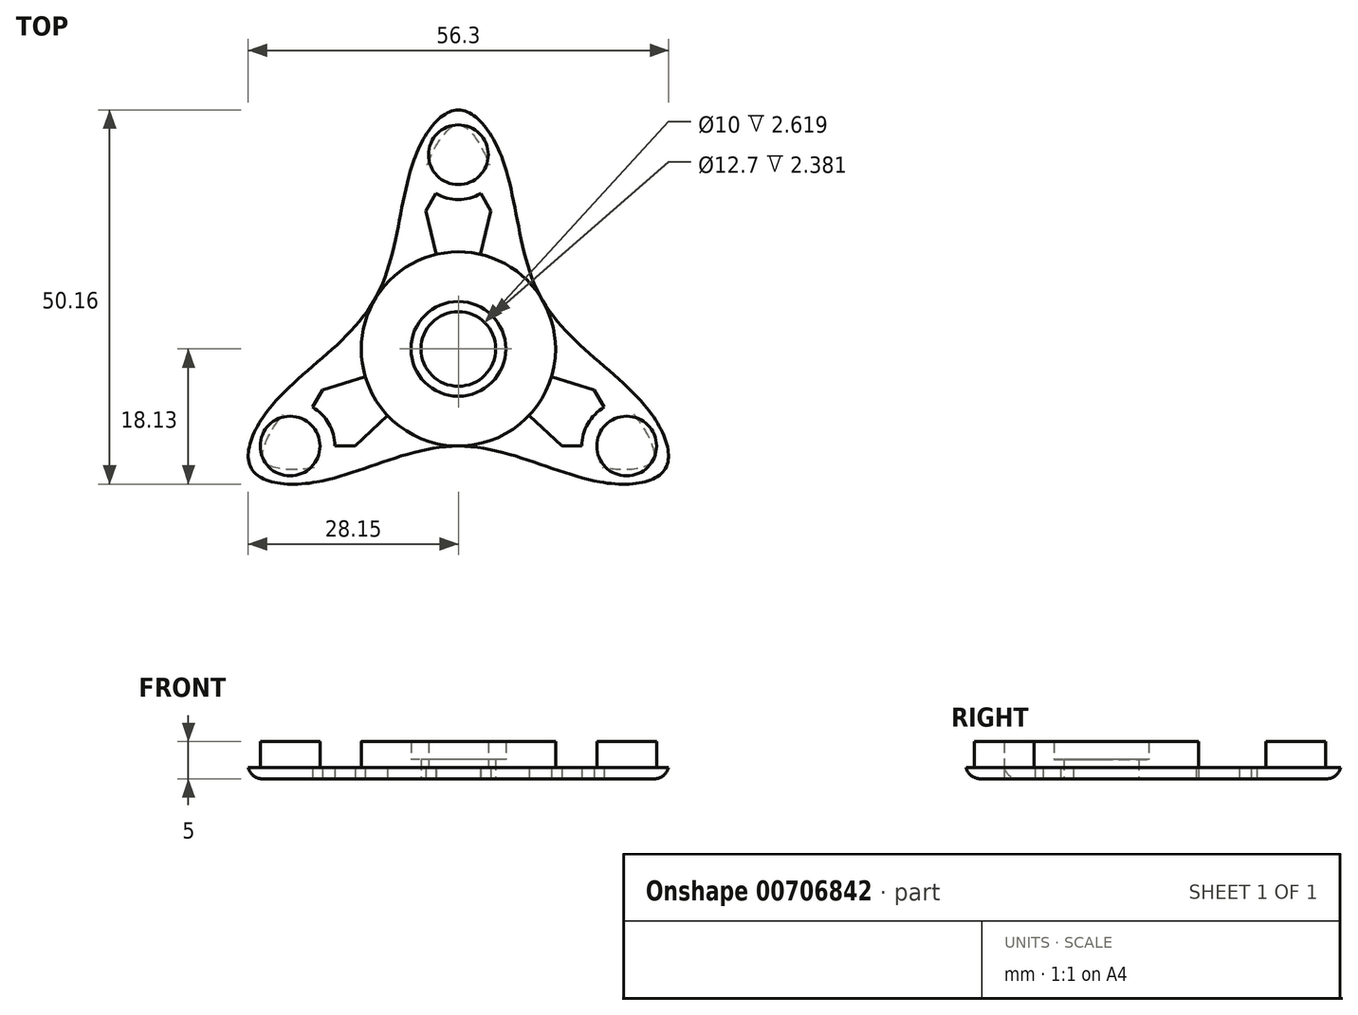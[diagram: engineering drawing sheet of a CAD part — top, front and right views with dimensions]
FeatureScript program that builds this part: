
annotation { "Feature Type Name" : "Feature", "Feature Type Description" : "" }
export const myFeature = defineFeature(function(context is Context, id is Id, definition is map)
    precondition{}
    {
        {
            var Q0;
            Q0=qCreatedBy(makeId("Top.planeOp"),FACE);
            var sketch = newSketch(context, id + "F0", { "sketchPlane" : qUnion([Q0])});
            skCircle(sketch, "E0", {"center": v(0, 0) * mm, "radius": 6.35 * mm});
            skCircle(sketch, "E1", {"center": v(0, 0) * mm, "radius": 26.03 * mm});
            skLineSegment(sketch, "E2", {"start": v(0, 0) * mm, "end": v(22.54, -13.01) * mm});
            skLineSegment(sketch, "E3", {"start": v(0, 0) * mm, "end": v(0, 26.03) * mm});
            skLineSegment(sketch, "E4", {"start": v(0, 26.03) * mm, "end": v(-22.54, -13.01) * mm});
            skLineSegment(sketch, "E5", {"start": v(0, 26.03) * mm, "end": v(22.54, -13.01) * mm});
            skLineSegment(sketch, "E6", {"start": v(22.54, -13.01) * mm, "end": v(-22.54, -13.01) * mm});
            skLineSegment(sketch, "E7", {"start": v(0, 0) * mm, "end": v(-22.54, -13.01) * mm});
            skCircle(sketch, "E8", {"center": v(0, 26.03) * mm, "radius": 4 * mm});
            skCircle(sketch, "E9", {"center": v(22.54, -13.01) * mm, "radius": 4 * mm});
            skCircle(sketch, "E10", {"center": v(-22.54, -13.01) * mm, "radius": 4 * mm});
            skLineSegment(sketch, "E11", {"start": v(0, 0) * mm, "end": v(-11.27, 6.5) * mm});
            skLineSegment(sketch, "E12", {"start": v(0, 0) * mm, "end": v(0, -13.01) * mm});
            skLineSegment(sketch, "E13", {"start": v(0, 0) * mm, "end": v(11.27, 6.5) * mm});
            skCircle(sketch, "E14", {"center": v(-22.54, -13.01) * mm, "radius": 6 * mm});
            skCircle(sketch, "E15", {"center": v(22.54, -13.01) * mm, "radius": 6 * mm});
            skCircle(sketch, "E16", {"center": v(0, 26.03) * mm, "radius": 6 * mm});
            skLineSegment(sketch, "E17", {"start": v(-24.92, -7.5) * mm, "end": v(0, 0) * mm});
            skLineSegment(sketch, "E18", {"start": v(-18.96, -17.83) * mm, "end": v(0, 0) * mm});
            skLineSegment(sketch, "E19", {"start": v(24.92, -7.5) * mm, "end": v(0, 0) * mm});
            skLineSegment(sketch, "E20", {"start": v(18.96, -17.83) * mm, "end": v(0, 0) * mm});
            skLineSegment(sketch, "E21", {"start": v(-5.96, 25.34) * mm, "end": v(0, 0) * mm});
            skLineSegment(sketch, "E22", {"start": v(5.96, 25.34) * mm, "end": v(0, 0) * mm});
            skLineSegment(sketch, "E23", {"start": v(0, 32.03) * mm, "end": v(0, 0) * mm});
            skLineSegment(sketch, "E24", {"start": v(0, 0) * mm, "end": v(-27.74, -16.01) * mm});
            skLineSegment(sketch, "E25", {"start": v(0, 0) * mm, "end": v(27.74, -16.01) * mm});
            skFitSpline(sketch, "E26", {"points": [v(-11.27, 6.5) * mm, v(-5.96, 25.34) * mm, v(0, 32.03) * mm, v(5.96, 25.34) * mm, v(11.27, 6.5) * mm, v(24.92, -7.5) * mm, v(27.74, -16.01) * mm, v(18.96, -17.83) * mm, v(0, -13.01) * mm, v(-18.96, -17.83) * mm, v(-27.74, -16.01) * mm, v(-24.92, -7.5) * mm, v(-11.27, 6.5) * mm]});
            skCircle(sketch, "E27", {"center": v(0, 0) * mm, "radius": 13.01 * mm});
            skCircle(sketch, "E28", {"center": v(0, 0) * mm, "radius": 5 * mm});
            skSolve(sketch);
        }
        {
            var Q0;
            {var subQ2=sQuery(id+"F0.wireOp",EDGE,"E1");var subQ4=sQuery(id+"F0.wireOp",EDGE,"E10");var subQ5=makeQuery(id+"F0.imprint","INTERSECT",VERTEX,{"disambiguationData":[OD(0.0)],"derivedFrom":[subQ2,subQ4]});Q0=makeQuery(id+"F0.imprint","IMPRINT",FACE,{"disambiguationData":[TD([[makeQuery(id+"F0.imprint","IMPRINT",EDGE,{"disambiguationData":[TD([[subQ5,-1.0]])],"derivedFrom":subQ4}),-1.0]])]});}
            var Q1;
            {var subQ2=sQuery(id+"F0.wireOp",EDGE,"E1");var subQ4=sQuery(id+"F0.wireOp",EDGE,"E10");var subQ5=makeQuery(id+"F0.imprint","INTERSECT",VERTEX,{"disambiguationData":[OD(1.0)],"derivedFrom":[subQ2,subQ4]});Q1=makeQuery(id+"F0.imprint","IMPRINT",FACE,{"disambiguationData":[TD([[makeQuery(id+"F0.imprint","IMPRINT",EDGE,{"disambiguationData":[TD([[subQ5,1.0]])],"derivedFrom":subQ4}),-1.0]])]});}
            var Q2;
            {var subQ0=sQuery(id+"F0.wireOp",EDGE,"E14");var subQ1=sQuery(id+"F0.wireOp",EDGE,"E6");var subQ2=makeQuery(id+"F0.imprint","INTERSECT",VERTEX,{"derivedFrom":[subQ1,subQ0]});Q2=makeQuery(id+"F0.imprint","IMPRINT",FACE,{"disambiguationData":[TD([[makeQuery(id+"F0.imprint","IMPRINT",EDGE,{"disambiguationData":[TD([[subQ2,-1.0]])],"derivedFrom":subQ1}),1.0]])]});}
            var Q3;
            {var subQ0=sQuery(id+"F0.wireOp",EDGE,"E14");var subQ1=sQuery(id+"F0.wireOp",EDGE,"E6");var subQ2=makeQuery(id+"F0.imprint","INTERSECT",VERTEX,{"derivedFrom":[subQ1,subQ0]});Q3=makeQuery(id+"F0.imprint","IMPRINT",FACE,{"disambiguationData":[TD([[makeQuery(id+"F0.imprint","IMPRINT",EDGE,{"disambiguationData":[TD([[subQ2,-1.0]])],"derivedFrom":subQ1}),-1.0]])]});}
            var Q4;
            {var subQ0=sQuery(id+"F0.wireOp",EDGE,"E14");var subQ1=sQuery(id+"F0.wireOp",EDGE,"E4");var subQ2=makeQuery(id+"F0.imprint","INTERSECT",VERTEX,{"derivedFrom":[subQ1,subQ0]});Q4=makeQuery(id+"F0.imprint","IMPRINT",FACE,{"disambiguationData":[TD([[makeQuery(id+"F0.imprint","IMPRINT",EDGE,{"disambiguationData":[TD([[subQ2,-1.0]])],"derivedFrom":subQ1}),1.0]])]});}
            var Q5;
            {var subQ3=sQuery(id+"F0.wireOp",EDGE,"E4");var subQ5=sQuery(id+"F0.wireOp",EDGE,"E14");var subQ6=makeQuery(id+"F0.imprint","INTERSECT",VERTEX,{"derivedFrom":[subQ3,subQ5]});Q5=makeQuery(id+"F0.imprint","IMPRINT",FACE,{"disambiguationData":[TD([[makeQuery(id+"F0.imprint","IMPRINT",EDGE,{"disambiguationData":[TD([[subQ6,-1.0]])],"derivedFrom":subQ3}),-1.0]])]});}
            var Q6;
            {var subQ0=sQuery(id+"F0.wireOp",EDGE,"E17");var subQ1=sQuery(id+"F0.wireOp",EDGE,"E4");var subQ2=makeQuery(id+"F0.imprint","INTERSECT",VERTEX,{"derivedFrom":[subQ1,subQ0]});Q6=makeQuery(id+"F0.imprint","IMPRINT",FACE,{"disambiguationData":[TD([[makeQuery(id+"F0.imprint","IMPRINT",EDGE,{"disambiguationData":[TD([[subQ2,-1.0]])],"derivedFrom":subQ1}),-1.0]])]});}
            var Q7;
            {var subQ0=sQuery(id+"F0.wireOp",EDGE,"E18");var subQ1=sQuery(id+"F0.wireOp",EDGE,"E6");var subQ2=makeQuery(id+"F0.imprint","INTERSECT",VERTEX,{"derivedFrom":[subQ1,subQ0]});Q7=makeQuery(id+"F0.imprint","IMPRINT",FACE,{"disambiguationData":[TD([[makeQuery(id+"F0.imprint","IMPRINT",EDGE,{"disambiguationData":[TD([[subQ2,-1.0]])],"derivedFrom":subQ1}),1.0]])]});}
            var Q8;
            {var subQ0=sQuery(id+"F0.wireOp",EDGE,"E17");var subQ1=sQuery(id+"F0.wireOp",EDGE,"E0");var subQ2=makeQuery(id+"F0.imprint","INTERSECT",VERTEX,{"derivedFrom":[subQ1,subQ0]});Q8=makeQuery(id+"F0.imprint","IMPRINT",FACE,{"disambiguationData":[TD([[makeQuery(id+"F0.imprint","IMPRINT",EDGE,{"disambiguationData":[TD([[subQ2,-1.0]])],"derivedFrom":subQ1}),-1.0]])]});}
            var Q9;
            {var subQ0=sQuery(id+"F0.wireOp",EDGE,"E24");var subQ1=sQuery(id+"F0.wireOp",EDGE,"E0");var subQ2=makeQuery(id+"F0.imprint","INTERSECT",VERTEX,{"derivedFrom":[subQ1,subQ0]});Q9=makeQuery(id+"F0.imprint","IMPRINT",FACE,{"disambiguationData":[TD([[makeQuery(id+"F0.imprint","IMPRINT",EDGE,{"disambiguationData":[TD([[subQ2,-1.0]])],"derivedFrom":subQ1}),-1.0]])]});}
            var Q10;
            {var subQ0=sQuery(id+"F0.wireOp",EDGE,"E11");var subQ1=sQuery(id+"F0.wireOp",EDGE,"E0");var subQ2=makeQuery(id+"F0.imprint","INTERSECT",VERTEX,{"derivedFrom":[subQ1,subQ0]});Q10=makeQuery(id+"F0.imprint","IMPRINT",FACE,{"disambiguationData":[TD([[makeQuery(id+"F0.imprint","IMPRINT",EDGE,{"disambiguationData":[TD([[subQ2,-1.0]])],"derivedFrom":subQ1}),-1.0]])]});}
            var Q11;
            {var subQ0=sQuery(id+"F0.wireOp",EDGE,"E18");var subQ1=sQuery(id+"F0.wireOp",EDGE,"E0");var subQ2=makeQuery(id+"F0.imprint","INTERSECT",VERTEX,{"derivedFrom":[subQ1,subQ0]});Q11=makeQuery(id+"F0.imprint","IMPRINT",FACE,{"disambiguationData":[TD([[makeQuery(id+"F0.imprint","IMPRINT",EDGE,{"disambiguationData":[TD([[subQ2,-1.0]])],"derivedFrom":subQ1}),-1.0]])]});}
            var Q12;
            {var subQ0=sQuery(id+"F0.wireOp",EDGE,"E12");var subQ1=sQuery(id+"F0.wireOp",EDGE,"E0");var subQ2=makeQuery(id+"F0.imprint","INTERSECT",VERTEX,{"derivedFrom":[subQ1,subQ0]});Q12=makeQuery(id+"F0.imprint","IMPRINT",FACE,{"disambiguationData":[TD([[makeQuery(id+"F0.imprint","IMPRINT",EDGE,{"disambiguationData":[TD([[subQ2,-1.0]])],"derivedFrom":subQ1}),-1.0]])]});}
            var Q13;
            {var subQ0=sQuery(id+"F0.wireOp",EDGE,"E20");var subQ1=sQuery(id+"F0.wireOp",EDGE,"E0");var subQ2=makeQuery(id+"F0.imprint","INTERSECT",VERTEX,{"derivedFrom":[subQ1,subQ0]});Q13=makeQuery(id+"F0.imprint","IMPRINT",FACE,{"disambiguationData":[TD([[makeQuery(id+"F0.imprint","IMPRINT",EDGE,{"disambiguationData":[TD([[subQ2,-1.0]])],"derivedFrom":subQ1}),-1.0]])]});}
            var Q14;
            {var subQ0=sQuery(id+"F0.wireOp",EDGE,"E25");var subQ1=sQuery(id+"F0.wireOp",EDGE,"E0");var subQ2=makeQuery(id+"F0.imprint","INTERSECT",VERTEX,{"derivedFrom":[subQ1,subQ0]});Q14=makeQuery(id+"F0.imprint","IMPRINT",FACE,{"disambiguationData":[TD([[makeQuery(id+"F0.imprint","IMPRINT",EDGE,{"disambiguationData":[TD([[subQ2,-1.0]])],"derivedFrom":subQ1}),-1.0]])]});}
            var Q15;
            {var subQ0=sQuery(id+"F0.wireOp",EDGE,"E13");var subQ1=sQuery(id+"F0.wireOp",EDGE,"E0");var subQ2=makeQuery(id+"F0.imprint","INTERSECT",VERTEX,{"derivedFrom":[subQ1,subQ0]});Q15=makeQuery(id+"F0.imprint","IMPRINT",FACE,{"disambiguationData":[TD([[makeQuery(id+"F0.imprint","IMPRINT",EDGE,{"disambiguationData":[TD([[subQ2,1.0]])],"derivedFrom":subQ1}),-1.0]])]});}
            var Q16;
            {var subQ0=sQuery(id+"F0.wireOp",EDGE,"E22");var subQ1=sQuery(id+"F0.wireOp",EDGE,"E0");var subQ2=makeQuery(id+"F0.imprint","INTERSECT",VERTEX,{"derivedFrom":[subQ1,subQ0]});Q16=makeQuery(id+"F0.imprint","IMPRINT",FACE,{"disambiguationData":[TD([[makeQuery(id+"F0.imprint","IMPRINT",EDGE,{"disambiguationData":[TD([[subQ2,1.0]])],"derivedFrom":subQ1}),-1.0]])]});}
            var Q17;
            {var subQ0=sQuery(id+"F0.wireOp",EDGE,"E21");var subQ1=sQuery(id+"F0.wireOp",EDGE,"E0");var subQ2=makeQuery(id+"F0.imprint","INTERSECT",VERTEX,{"derivedFrom":[subQ1,subQ0]});Q17=makeQuery(id+"F0.imprint","IMPRINT",FACE,{"disambiguationData":[TD([[makeQuery(id+"F0.imprint","IMPRINT",EDGE,{"disambiguationData":[TD([[subQ2,-1.0]])],"derivedFrom":subQ1}),-1.0]])]});}
            var Q18;
            {var subQ0=sQuery(id+"F0.wireOp",EDGE,"E23");var subQ1=sQuery(id+"F0.wireOp",EDGE,"E0");var subQ2=makeQuery(id+"F0.imprint","INTERSECT",VERTEX,{"derivedFrom":[subQ1,subQ0]});Q18=makeQuery(id+"F0.imprint","IMPRINT",FACE,{"disambiguationData":[TD([[makeQuery(id+"F0.imprint","IMPRINT",EDGE,{"disambiguationData":[TD([[subQ2,-1.0]])],"derivedFrom":subQ1}),-1.0]])]});}
            var Q19;
            {var subQ0=sQuery(id+"F0.wireOp",EDGE,"E22");var subQ1=sQuery(id+"F0.wireOp",EDGE,"E0");var subQ2=makeQuery(id+"F0.imprint","INTERSECT",VERTEX,{"derivedFrom":[subQ1,subQ0]});Q19=makeQuery(id+"F0.imprint","IMPRINT",FACE,{"disambiguationData":[TD([[makeQuery(id+"F0.imprint","IMPRINT",EDGE,{"disambiguationData":[TD([[subQ2,-1.0]])],"derivedFrom":subQ1}),-1.0]])]});}
            var Q20;
            {var subQ1=sQuery(id+"F0.wireOp",EDGE,"E4");var subQ3=sQuery(id+"F0.wireOp",EDGE,"E17");var subQ4=makeQuery(id+"F0.imprint","INTERSECT",VERTEX,{"derivedFrom":[subQ1,subQ3]});Q20=makeQuery(id+"F0.imprint","IMPRINT",FACE,{"disambiguationData":[TD([[makeQuery(id+"F0.imprint","IMPRINT",EDGE,{"disambiguationData":[TD([[subQ4,-1.0]])],"derivedFrom":subQ3}),1.0]])]});}
            var Q21;
            {var subQ1=sQuery(id+"F0.wireOp",EDGE,"E6");var subQ3=sQuery(id+"F0.wireOp",EDGE,"E18");var subQ4=makeQuery(id+"F0.imprint","INTERSECT",VERTEX,{"derivedFrom":[subQ1,subQ3]});Q21=makeQuery(id+"F0.imprint","IMPRINT",FACE,{"disambiguationData":[TD([[makeQuery(id+"F0.imprint","IMPRINT",EDGE,{"disambiguationData":[TD([[subQ4,-1.0]])],"derivedFrom":subQ3}),-1.0]])]});}
            var Q22;
            {var subQ1=sQuery(id+"F0.wireOp",EDGE,"E6");var subQ3=sQuery(id+"F0.wireOp",EDGE,"E20");var subQ4=makeQuery(id+"F0.imprint","INTERSECT",VERTEX,{"derivedFrom":[subQ1,subQ3]});Q22=makeQuery(id+"F0.imprint","IMPRINT",FACE,{"disambiguationData":[TD([[makeQuery(id+"F0.imprint","IMPRINT",EDGE,{"disambiguationData":[TD([[subQ4,-1.0]])],"derivedFrom":subQ3}),1.0]])]});}
            var Q23;
            {var subQ0=sQuery(id+"F0.wireOp",EDGE,"E15");var subQ1=sQuery(id+"F0.wireOp",EDGE,"E5");var subQ2=makeQuery(id+"F0.imprint","INTERSECT",VERTEX,{"derivedFrom":[subQ1,subQ0]});Q23=makeQuery(id+"F0.imprint","IMPRINT",FACE,{"disambiguationData":[TD([[makeQuery(id+"F0.imprint","IMPRINT",EDGE,{"disambiguationData":[TD([[subQ2,-1.0]])],"derivedFrom":subQ1}),-1.0]])]});}
            var Q24;
            {var subQ0=sQuery(id+"F0.wireOp",EDGE,"E9");var subQ1=sQuery(id+"F0.wireOp",EDGE,"E6");var subQ2=makeQuery(id+"F0.imprint","INTERSECT",VERTEX,{"derivedFrom":[subQ1,subQ0]});Q24=makeQuery(id+"F0.imprint","IMPRINT",FACE,{"disambiguationData":[TD([[makeQuery(id+"F0.imprint","IMPRINT",EDGE,{"disambiguationData":[TD([[subQ2,-1.0]])],"derivedFrom":subQ1}),-1.0]])]});}
            var Q25;
            {var subQ0=sQuery(id+"F0.wireOp",EDGE,"E9");var subQ3=sQuery(id+"F0.wireOp",EDGE,"E6");var subQ4=makeQuery(id+"F0.imprint","INTERSECT",VERTEX,{"derivedFrom":[subQ3,subQ0]});Q25=makeQuery(id+"F0.imprint","IMPRINT",FACE,{"disambiguationData":[TD([[makeQuery(id+"F0.imprint","IMPRINT",EDGE,{"disambiguationData":[TD([[subQ4,-1.0]])],"derivedFrom":subQ3}),1.0]])]});}
            var Q26;
            {var subQ2=sQuery(id+"F0.wireOp",EDGE,"E1");var subQ4=sQuery(id+"F0.wireOp",EDGE,"E9");var subQ5=makeQuery(id+"F0.imprint","INTERSECT",VERTEX,{"disambiguationData":[OD(0.0)],"derivedFrom":[subQ2,subQ4]});Q26=makeQuery(id+"F0.imprint","IMPRINT",FACE,{"disambiguationData":[TD([[makeQuery(id+"F0.imprint","IMPRINT",EDGE,{"disambiguationData":[TD([[subQ5,-1.0]])],"derivedFrom":subQ4}),-1.0]])]});}
            var Q27;
            {var subQ2=sQuery(id+"F0.wireOp",EDGE,"E1");var subQ4=sQuery(id+"F0.wireOp",EDGE,"E9");var subQ5=makeQuery(id+"F0.imprint","INTERSECT",VERTEX,{"disambiguationData":[OD(1.0)],"derivedFrom":[subQ2,subQ4]});Q27=makeQuery(id+"F0.imprint","IMPRINT",FACE,{"disambiguationData":[TD([[makeQuery(id+"F0.imprint","IMPRINT",EDGE,{"disambiguationData":[TD([[subQ5,1.0]])],"derivedFrom":subQ4}),-1.0]])]});}
            var Q28;
            {var subQ0=sQuery(id+"F0.wireOp",EDGE,"E15");var subQ1=sQuery(id+"F0.wireOp",EDGE,"E5");var subQ2=makeQuery(id+"F0.imprint","INTERSECT",VERTEX,{"derivedFrom":[subQ1,subQ0]});Q28=makeQuery(id+"F0.imprint","IMPRINT",FACE,{"disambiguationData":[TD([[makeQuery(id+"F0.imprint","IMPRINT",EDGE,{"disambiguationData":[TD([[subQ2,-1.0]])],"derivedFrom":subQ1}),1.0]])]});}
            var Q29;
            {var subQ0=sQuery(id+"F0.wireOp",EDGE,"E19");var subQ1=sQuery(id+"F0.wireOp",EDGE,"E5");var subQ2=makeQuery(id+"F0.imprint","INTERSECT",VERTEX,{"derivedFrom":[subQ1,subQ0]});Q29=makeQuery(id+"F0.imprint","IMPRINT",FACE,{"disambiguationData":[TD([[makeQuery(id+"F0.imprint","IMPRINT",EDGE,{"disambiguationData":[TD([[subQ2,-1.0]])],"derivedFrom":subQ1}),1.0]])]});}
            var Q30;
            {var subQ1=sQuery(id+"F0.wireOp",EDGE,"E5");var subQ3=sQuery(id+"F0.wireOp",EDGE,"E19");var subQ4=makeQuery(id+"F0.imprint","INTERSECT",VERTEX,{"derivedFrom":[subQ1,subQ3]});Q30=makeQuery(id+"F0.imprint","IMPRINT",FACE,{"disambiguationData":[TD([[makeQuery(id+"F0.imprint","IMPRINT",EDGE,{"disambiguationData":[TD([[subQ4,-1.0]])],"derivedFrom":subQ3}),-1.0]])]});}
            var Q31;
            {var subQ1=sQuery(id+"F0.wireOp",EDGE,"E4");var subQ3=sQuery(id+"F0.wireOp",EDGE,"E21");var subQ4=makeQuery(id+"F0.imprint","INTERSECT",VERTEX,{"derivedFrom":[subQ1,subQ3]});Q31=makeQuery(id+"F0.imprint","IMPRINT",FACE,{"disambiguationData":[TD([[makeQuery(id+"F0.imprint","IMPRINT",EDGE,{"disambiguationData":[TD([[subQ4,-1.0]])],"derivedFrom":subQ3}),-1.0]])]});}
            var Q32;
            {var subQ0=sQuery(id+"F0.wireOp",EDGE,"E8");var subQ3=sQuery(id+"F0.wireOp",EDGE,"E5");var subQ4=makeQuery(id+"F0.imprint","INTERSECT",VERTEX,{"derivedFrom":[subQ3,subQ0]});Q32=makeQuery(id+"F0.imprint","IMPRINT",FACE,{"disambiguationData":[TD([[makeQuery(id+"F0.imprint","IMPRINT",EDGE,{"disambiguationData":[TD([[subQ4,-1.0]])],"derivedFrom":subQ3}),1.0]])]});}
            var Q33;
            {var subQ0=sQuery(id+"F0.wireOp",EDGE,"E8");var subQ1=sQuery(id+"F0.wireOp",EDGE,"E5");var subQ2=makeQuery(id+"F0.imprint","INTERSECT",VERTEX,{"derivedFrom":[subQ1,subQ0]});Q33=makeQuery(id+"F0.imprint","IMPRINT",FACE,{"disambiguationData":[TD([[makeQuery(id+"F0.imprint","IMPRINT",EDGE,{"disambiguationData":[TD([[subQ2,-1.0]])],"derivedFrom":subQ1}),-1.0]])]});}
            var Q34;
            {var subQ0=sQuery(id+"F0.wireOp",EDGE,"E16");var subQ1=sQuery(id+"F0.wireOp",EDGE,"E4");var subQ2=makeQuery(id+"F0.imprint","INTERSECT",VERTEX,{"derivedFrom":[subQ1,subQ0]});Q34=makeQuery(id+"F0.imprint","IMPRINT",FACE,{"disambiguationData":[TD([[makeQuery(id+"F0.imprint","IMPRINT",EDGE,{"disambiguationData":[TD([[subQ2,-1.0]])],"derivedFrom":subQ1}),-1.0]])]});}
            var Q35;
            {var subQ2=sQuery(id+"F0.wireOp",EDGE,"E1");var subQ4=sQuery(id+"F0.wireOp",EDGE,"E8");var subQ5=makeQuery(id+"F0.imprint","INTERSECT",VERTEX,{"disambiguationData":[OD(1.0)],"derivedFrom":[subQ2,subQ4]});Q35=makeQuery(id+"F0.imprint","IMPRINT",FACE,{"disambiguationData":[TD([[makeQuery(id+"F0.imprint","IMPRINT",EDGE,{"disambiguationData":[TD([[subQ5,1.0]])],"derivedFrom":subQ4}),-1.0]])]});}
            var Q36;
            {var subQ2=sQuery(id+"F0.wireOp",EDGE,"E1");var subQ4=sQuery(id+"F0.wireOp",EDGE,"E8");var subQ5=makeQuery(id+"F0.imprint","INTERSECT",VERTEX,{"disambiguationData":[OD(0.0)],"derivedFrom":[subQ2,subQ4]});Q36=makeQuery(id+"F0.imprint","IMPRINT",FACE,{"disambiguationData":[TD([[makeQuery(id+"F0.imprint","IMPRINT",EDGE,{"disambiguationData":[TD([[subQ5,-1.0]])],"derivedFrom":subQ4}),-1.0]])]});}
            var Q37;
            {var subQ0=sQuery(id+"F0.wireOp",EDGE,"E15");var subQ1=sQuery(id+"F0.wireOp",EDGE,"E6");var subQ2=makeQuery(id+"F0.imprint","INTERSECT",VERTEX,{"derivedFrom":[subQ1,subQ0]});Q37=makeQuery(id+"F0.imprint","IMPRINT",FACE,{"disambiguationData":[TD([[makeQuery(id+"F0.imprint","IMPRINT",EDGE,{"disambiguationData":[TD([[subQ2,-1.0]])],"derivedFrom":subQ1}),1.0]])]});}
            var Q38;
            {var subQ0=sQuery(id+"F0.wireOp",EDGE,"E8");var subQ3=sQuery(id+"F0.wireOp",EDGE,"E4");var subQ4=makeQuery(id+"F0.imprint","INTERSECT",VERTEX,{"derivedFrom":[subQ3,subQ0]});Q38=makeQuery(id+"F0.imprint","IMPRINT",FACE,{"disambiguationData":[TD([[makeQuery(id+"F0.imprint","IMPRINT",EDGE,{"disambiguationData":[TD([[subQ4,-1.0]])],"derivedFrom":subQ3}),-1.0]])]});}
            var Q39;
            {var subQ0=sQuery(id+"F0.wireOp",EDGE,"E8");var subQ1=sQuery(id+"F0.wireOp",EDGE,"E4");var subQ2=makeQuery(id+"F0.imprint","INTERSECT",VERTEX,{"derivedFrom":[subQ1,subQ0]});Q39=makeQuery(id+"F0.imprint","IMPRINT",FACE,{"disambiguationData":[TD([[makeQuery(id+"F0.imprint","IMPRINT",EDGE,{"disambiguationData":[TD([[subQ2,-1.0]])],"derivedFrom":subQ1}),1.0]])]});}
            var Q40;
            {var subQ0=sQuery(id+"F0.wireOp",EDGE,"E16");var subQ1=sQuery(id+"F0.wireOp",EDGE,"E5");var subQ2=makeQuery(id+"F0.imprint","INTERSECT",VERTEX,{"derivedFrom":[subQ1,subQ0]});Q40=makeQuery(id+"F0.imprint","IMPRINT",FACE,{"disambiguationData":[TD([[makeQuery(id+"F0.imprint","IMPRINT",EDGE,{"disambiguationData":[TD([[subQ2,-1.0]])],"derivedFrom":subQ1}),1.0]])]});}
            var Q41;
            {var subQ1=sQuery(id+"F0.wireOp",EDGE,"E5");var subQ3=sQuery(id+"F0.wireOp",EDGE,"E22");var subQ4=makeQuery(id+"F0.imprint","INTERSECT",VERTEX,{"derivedFrom":[subQ1,subQ3]});Q41=makeQuery(id+"F0.imprint","IMPRINT",FACE,{"disambiguationData":[TD([[makeQuery(id+"F0.imprint","IMPRINT",EDGE,{"disambiguationData":[TD([[subQ4,-1.0]])],"derivedFrom":subQ3}),1.0]])]});}
            var Q42;
            {var subQ1=sQuery(id+"F0.wireOp",EDGE,"E4");var subQ3=sQuery(id+"F0.wireOp",EDGE,"E21");var subQ4=makeQuery(id+"F0.imprint","INTERSECT",VERTEX,{"derivedFrom":[subQ1,subQ3]});Q42=makeQuery(id+"F0.imprint","IMPRINT",FACE,{"disambiguationData":[TD([[makeQuery(id+"F0.imprint","IMPRINT",EDGE,{"disambiguationData":[TD([[subQ4,1.0]])],"derivedFrom":subQ3}),-1.0]])]});}
            var Q43;
            {var subQ1=sQuery(id+"F0.wireOp",EDGE,"E4");var subQ3=sQuery(id+"F0.wireOp",EDGE,"E17");var subQ4=makeQuery(id+"F0.imprint","INTERSECT",VERTEX,{"derivedFrom":[subQ1,subQ3]});Q43=makeQuery(id+"F0.imprint","IMPRINT",FACE,{"disambiguationData":[TD([[makeQuery(id+"F0.imprint","IMPRINT",EDGE,{"disambiguationData":[TD([[subQ4,1.0]])],"derivedFrom":subQ3}),1.0]])]});}
            var Q44;
            {var subQ1=sQuery(id+"F0.wireOp",EDGE,"E5");var subQ3=sQuery(id+"F0.wireOp",EDGE,"E22");var subQ4=makeQuery(id+"F0.imprint","INTERSECT",VERTEX,{"derivedFrom":[subQ1,subQ3]});Q44=makeQuery(id+"F0.imprint","IMPRINT",FACE,{"disambiguationData":[TD([[makeQuery(id+"F0.imprint","IMPRINT",EDGE,{"disambiguationData":[TD([[subQ4,1.0]])],"derivedFrom":subQ3}),1.0]])]});}
            var Q45;
            {var subQ1=sQuery(id+"F0.wireOp",EDGE,"E6");var subQ3=sQuery(id+"F0.wireOp",EDGE,"E20");var subQ4=makeQuery(id+"F0.imprint","INTERSECT",VERTEX,{"derivedFrom":[subQ1,subQ3]});Q45=makeQuery(id+"F0.imprint","IMPRINT",FACE,{"disambiguationData":[TD([[makeQuery(id+"F0.imprint","IMPRINT",EDGE,{"disambiguationData":[TD([[subQ4,1.0]])],"derivedFrom":subQ3}),1.0]])]});}
            var Q46;
            {var subQ1=sQuery(id+"F0.wireOp",EDGE,"E5");var subQ3=sQuery(id+"F0.wireOp",EDGE,"E19");var subQ4=makeQuery(id+"F0.imprint","INTERSECT",VERTEX,{"derivedFrom":[subQ1,subQ3]});Q46=makeQuery(id+"F0.imprint","IMPRINT",FACE,{"disambiguationData":[TD([[makeQuery(id+"F0.imprint","IMPRINT",EDGE,{"disambiguationData":[TD([[subQ4,1.0]])],"derivedFrom":subQ3}),-1.0]])]});}
            var Q47;
            {var subQ1=sQuery(id+"F0.wireOp",EDGE,"E1");var subQ3=sQuery(id+"F0.wireOp",EDGE,"E10");var subQ4=makeQuery(id+"F0.imprint","INTERSECT",VERTEX,{"disambiguationData":[OD(0.0)],"derivedFrom":[subQ1,subQ3]});Q47=makeQuery(id+"F0.imprint","IMPRINT",FACE,{"disambiguationData":[TD([[makeQuery(id+"F0.imprint","IMPRINT",EDGE,{"disambiguationData":[TD([[subQ4,1.0]])],"derivedFrom":subQ3}),1.0]])]});}
            var Q48;
            {var subQ1=sQuery(id+"F0.wireOp",EDGE,"E1");var subQ3=sQuery(id+"F0.wireOp",EDGE,"E10");var subQ4=makeQuery(id+"F0.imprint","INTERSECT",VERTEX,{"disambiguationData":[OD(0.0)],"derivedFrom":[subQ1,subQ3]});Q48=makeQuery(id+"F0.imprint","IMPRINT",FACE,{"disambiguationData":[TD([[makeQuery(id+"F0.imprint","IMPRINT",EDGE,{"disambiguationData":[TD([[subQ4,-1.0]])],"derivedFrom":subQ3}),1.0]])]});}
            var Q49;
            {var subQ1=sQuery(id+"F0.wireOp",EDGE,"E1");var subQ3=sQuery(id+"F0.wireOp",EDGE,"E10");var subQ4=makeQuery(id+"F0.imprint","INTERSECT",VERTEX,{"disambiguationData":[OD(1.0)],"derivedFrom":[subQ1,subQ3]});Q49=makeQuery(id+"F0.imprint","IMPRINT",FACE,{"disambiguationData":[TD([[makeQuery(id+"F0.imprint","IMPRINT",EDGE,{"disambiguationData":[TD([[subQ4,1.0]])],"derivedFrom":subQ3}),1.0]])]});}
            var Q50;
            {var subQ1=sQuery(id+"F0.wireOp",EDGE,"E1");var subQ3=sQuery(id+"F0.wireOp",EDGE,"E10");var subQ4=makeQuery(id+"F0.imprint","INTERSECT",VERTEX,{"disambiguationData":[OD(1.0)],"derivedFrom":[subQ1,subQ3]});Q50=makeQuery(id+"F0.imprint","IMPRINT",FACE,{"disambiguationData":[TD([[makeQuery(id+"F0.imprint","IMPRINT",EDGE,{"disambiguationData":[TD([[subQ4,-1.0]])],"derivedFrom":subQ3}),1.0]])]});}
            var Q51;
            {var subQ1=sQuery(id+"F0.wireOp",EDGE,"E6");var subQ3=sQuery(id+"F0.wireOp",EDGE,"E10");var subQ4=makeQuery(id+"F0.imprint","INTERSECT",VERTEX,{"derivedFrom":[subQ1,subQ3]});Q51=makeQuery(id+"F0.imprint","IMPRINT",FACE,{"disambiguationData":[TD([[makeQuery(id+"F0.imprint","IMPRINT",EDGE,{"disambiguationData":[TD([[subQ4,-1.0]])],"derivedFrom":subQ3}),1.0]])]});}
            var Q52;
            {var subQ1=sQuery(id+"F0.wireOp",EDGE,"E4");var subQ3=sQuery(id+"F0.wireOp",EDGE,"E10");var subQ4=makeQuery(id+"F0.imprint","INTERSECT",VERTEX,{"derivedFrom":[subQ1,subQ3]});Q52=makeQuery(id+"F0.imprint","IMPRINT",FACE,{"disambiguationData":[TD([[makeQuery(id+"F0.imprint","IMPRINT",EDGE,{"disambiguationData":[TD([[subQ4,1.0]])],"derivedFrom":subQ3}),1.0]])]});}
            var Q53;
            {var subQ1=sQuery(id+"F0.wireOp",EDGE,"E6");var subQ3=sQuery(id+"F0.wireOp",EDGE,"E9");var subQ4=makeQuery(id+"F0.imprint","INTERSECT",VERTEX,{"derivedFrom":[subQ1,subQ3]});Q53=makeQuery(id+"F0.imprint","IMPRINT",FACE,{"disambiguationData":[TD([[makeQuery(id+"F0.imprint","IMPRINT",EDGE,{"disambiguationData":[TD([[subQ4,1.0]])],"derivedFrom":subQ3}),1.0]])]});}
            var Q54;
            {var subQ1=sQuery(id+"F0.wireOp",EDGE,"E5");var subQ3=sQuery(id+"F0.wireOp",EDGE,"E9");var subQ4=makeQuery(id+"F0.imprint","INTERSECT",VERTEX,{"derivedFrom":[subQ1,subQ3]});Q54=makeQuery(id+"F0.imprint","IMPRINT",FACE,{"disambiguationData":[TD([[makeQuery(id+"F0.imprint","IMPRINT",EDGE,{"disambiguationData":[TD([[subQ4,-1.0]])],"derivedFrom":subQ3}),1.0]])]});}
            var Q55;
            {var subQ1=sQuery(id+"F0.wireOp",EDGE,"E1");var subQ3=sQuery(id+"F0.wireOp",EDGE,"E9");var subQ4=makeQuery(id+"F0.imprint","INTERSECT",VERTEX,{"disambiguationData":[OD(1.0)],"derivedFrom":[subQ1,subQ3]});Q55=makeQuery(id+"F0.imprint","IMPRINT",FACE,{"disambiguationData":[TD([[makeQuery(id+"F0.imprint","IMPRINT",EDGE,{"disambiguationData":[TD([[subQ4,-1.0]])],"derivedFrom":subQ3}),1.0]])]});}
            var Q56;
            {var subQ1=sQuery(id+"F0.wireOp",EDGE,"E1");var subQ3=sQuery(id+"F0.wireOp",EDGE,"E9");var subQ4=makeQuery(id+"F0.imprint","INTERSECT",VERTEX,{"disambiguationData":[OD(0.0)],"derivedFrom":[subQ1,subQ3]});Q56=makeQuery(id+"F0.imprint","IMPRINT",FACE,{"disambiguationData":[TD([[makeQuery(id+"F0.imprint","IMPRINT",EDGE,{"disambiguationData":[TD([[subQ4,-1.0]])],"derivedFrom":subQ3}),1.0]])]});}
            var Q57;
            {var subQ1=sQuery(id+"F0.wireOp",EDGE,"E1");var subQ3=sQuery(id+"F0.wireOp",EDGE,"E9");var subQ4=makeQuery(id+"F0.imprint","INTERSECT",VERTEX,{"disambiguationData":[OD(0.0)],"derivedFrom":[subQ1,subQ3]});Q57=makeQuery(id+"F0.imprint","IMPRINT",FACE,{"disambiguationData":[TD([[makeQuery(id+"F0.imprint","IMPRINT",EDGE,{"disambiguationData":[TD([[subQ4,1.0]])],"derivedFrom":subQ3}),1.0]])]});}
            var Q58;
            {var subQ1=sQuery(id+"F0.wireOp",EDGE,"E5");var subQ3=sQuery(id+"F0.wireOp",EDGE,"E8");var subQ4=makeQuery(id+"F0.imprint","INTERSECT",VERTEX,{"derivedFrom":[subQ1,subQ3]});Q58=makeQuery(id+"F0.imprint","IMPRINT",FACE,{"disambiguationData":[TD([[makeQuery(id+"F0.imprint","IMPRINT",EDGE,{"disambiguationData":[TD([[subQ4,1.0]])],"derivedFrom":subQ3}),1.0]])]});}
            var Q59;
            {var subQ1=sQuery(id+"F0.wireOp",EDGE,"E4");var subQ3=sQuery(id+"F0.wireOp",EDGE,"E8");var subQ4=makeQuery(id+"F0.imprint","INTERSECT",VERTEX,{"derivedFrom":[subQ1,subQ3]});Q59=makeQuery(id+"F0.imprint","IMPRINT",FACE,{"disambiguationData":[TD([[makeQuery(id+"F0.imprint","IMPRINT",EDGE,{"disambiguationData":[TD([[subQ4,-1.0]])],"derivedFrom":subQ3}),1.0]])]});}
            var Q60;
            {var subQ1=sQuery(id+"F0.wireOp",EDGE,"E1");var subQ3=sQuery(id+"F0.wireOp",EDGE,"E8");var subQ4=makeQuery(id+"F0.imprint","INTERSECT",VERTEX,{"disambiguationData":[OD(1.0)],"derivedFrom":[subQ1,subQ3]});Q60=makeQuery(id+"F0.imprint","IMPRINT",FACE,{"disambiguationData":[TD([[makeQuery(id+"F0.imprint","IMPRINT",EDGE,{"disambiguationData":[TD([[subQ4,1.0]])],"derivedFrom":subQ3}),1.0]])]});}
            var Q61;
            {var subQ1=sQuery(id+"F0.wireOp",EDGE,"E1");var subQ3=sQuery(id+"F0.wireOp",EDGE,"E8");var subQ4=makeQuery(id+"F0.imprint","INTERSECT",VERTEX,{"disambiguationData":[OD(0.0)],"derivedFrom":[subQ1,subQ3]});Q61=makeQuery(id+"F0.imprint","IMPRINT",FACE,{"disambiguationData":[TD([[makeQuery(id+"F0.imprint","IMPRINT",EDGE,{"disambiguationData":[TD([[subQ4,1.0]])],"derivedFrom":subQ3}),1.0]])]});}
            var Q62;
            {var subQ1=sQuery(id+"F0.wireOp",EDGE,"E1");var subQ3=sQuery(id+"F0.wireOp",EDGE,"E8");var subQ4=makeQuery(id+"F0.imprint","INTERSECT",VERTEX,{"disambiguationData":[OD(0.0)],"derivedFrom":[subQ1,subQ3]});Q62=makeQuery(id+"F0.imprint","IMPRINT",FACE,{"disambiguationData":[TD([[makeQuery(id+"F0.imprint","IMPRINT",EDGE,{"disambiguationData":[TD([[subQ4,-1.0]])],"derivedFrom":subQ3}),1.0]])]});}
            var Q63;
            {var subQ1=sQuery(id+"F0.wireOp",EDGE,"E1");var subQ3=sQuery(id+"F0.wireOp",EDGE,"E9");var subQ4=makeQuery(id+"F0.imprint","INTERSECT",VERTEX,{"disambiguationData":[OD(1.0)],"derivedFrom":[subQ1,subQ3]});Q63=makeQuery(id+"F0.imprint","IMPRINT",FACE,{"disambiguationData":[TD([[makeQuery(id+"F0.imprint","IMPRINT",EDGE,{"disambiguationData":[TD([[subQ4,1.0]])],"derivedFrom":subQ3}),1.0]])]});}
            var Q64;
            {var subQ1=sQuery(id+"F0.wireOp",EDGE,"E1");var subQ3=sQuery(id+"F0.wireOp",EDGE,"E8");var subQ4=makeQuery(id+"F0.imprint","INTERSECT",VERTEX,{"disambiguationData":[OD(1.0)],"derivedFrom":[subQ1,subQ3]});Q64=makeQuery(id+"F0.imprint","IMPRINT",FACE,{"disambiguationData":[TD([[makeQuery(id+"F0.imprint","IMPRINT",EDGE,{"disambiguationData":[TD([[subQ4,-1.0]])],"derivedFrom":subQ3}),1.0]])]});}
            var Q65;
            {var subQ0=sQuery(id+"F0.wireOp",EDGE,"E17");var subQ1=sQuery(id+"F0.wireOp",EDGE,"E14");var subQ3=makeQuery(id+"F0.imprint","INTERSECT",VERTEX,{"derivedFrom":[subQ1,subQ0]});Q65=makeQuery(id+"F0.imprint","IMPRINT",FACE,{"disambiguationData":[TD([[makeQuery(id+"F0.imprint","IMPRINT",EDGE,{"disambiguationData":[TD([[subQ3,-1.0]])],"derivedFrom":subQ1}),1.0]])]});}
            var Q66;
            {var subQ0=sQuery(id+"F0.wireOp",EDGE,"E18");var subQ1=sQuery(id+"F0.wireOp",EDGE,"E14");var subQ3=makeQuery(id+"F0.imprint","INTERSECT",VERTEX,{"derivedFrom":[subQ1,subQ0]});Q66=makeQuery(id+"F0.imprint","IMPRINT",FACE,{"disambiguationData":[TD([[makeQuery(id+"F0.imprint","IMPRINT",EDGE,{"disambiguationData":[TD([[subQ3,1.0]])],"derivedFrom":subQ1}),1.0]])]});}
            var Q67;
            {var subQ0=sQuery(id+"F0.wireOp",EDGE,"E20");var subQ1=sQuery(id+"F0.wireOp",EDGE,"E15");var subQ3=makeQuery(id+"F0.imprint","INTERSECT",VERTEX,{"derivedFrom":[subQ1,subQ0]});Q67=makeQuery(id+"F0.imprint","IMPRINT",FACE,{"disambiguationData":[TD([[makeQuery(id+"F0.imprint","IMPRINT",EDGE,{"disambiguationData":[TD([[subQ3,-1.0]])],"derivedFrom":subQ1}),1.0]])]});}
            var Q68;
            {var subQ0=sQuery(id+"F0.wireOp",EDGE,"E19");var subQ1=sQuery(id+"F0.wireOp",EDGE,"E15");var subQ3=makeQuery(id+"F0.imprint","INTERSECT",VERTEX,{"derivedFrom":[subQ1,subQ0]});Q68=makeQuery(id+"F0.imprint","IMPRINT",FACE,{"disambiguationData":[TD([[makeQuery(id+"F0.imprint","IMPRINT",EDGE,{"disambiguationData":[TD([[subQ3,1.0]])],"derivedFrom":subQ1}),1.0]])]});}
            var Q69;
            {var subQ1=sQuery(id+"F0.wireOp",EDGE,"E6");var subQ3=sQuery(id+"F0.wireOp",EDGE,"E18");var subQ4=makeQuery(id+"F0.imprint","INTERSECT",VERTEX,{"derivedFrom":[subQ1,subQ3]});Q69=makeQuery(id+"F0.imprint","IMPRINT",FACE,{"disambiguationData":[TD([[makeQuery(id+"F0.imprint","IMPRINT",EDGE,{"disambiguationData":[TD([[subQ4,1.0]])],"derivedFrom":subQ3}),-1.0]])]});}
            var Q70;
            {var subQ0=sQuery(id+"F0.wireOp",EDGE,"E22");var subQ1=sQuery(id+"F0.wireOp",EDGE,"E16");var subQ3=makeQuery(id+"F0.imprint","INTERSECT",VERTEX,{"derivedFrom":[subQ1,subQ0]});Q70=makeQuery(id+"F0.imprint","IMPRINT",FACE,{"disambiguationData":[TD([[makeQuery(id+"F0.imprint","IMPRINT",EDGE,{"disambiguationData":[TD([[subQ3,-1.0]])],"derivedFrom":subQ1}),1.0]])]});}
            var Q71;
            {var subQ0=sQuery(id+"F0.wireOp",EDGE,"E21");var subQ1=sQuery(id+"F0.wireOp",EDGE,"E16");var subQ3=makeQuery(id+"F0.imprint","INTERSECT",VERTEX,{"derivedFrom":[subQ1,subQ0]});Q71=makeQuery(id+"F0.imprint","IMPRINT",FACE,{"disambiguationData":[TD([[makeQuery(id+"F0.imprint","IMPRINT",EDGE,{"disambiguationData":[TD([[subQ3,1.0]])],"derivedFrom":subQ1}),1.0]])]});}
            var Q72;
            {var subQ0=sQuery(id+"F0.wireOp",EDGE,"E11");var subQ1=sQuery(id+"F0.wireOp",EDGE,"E0");var subQ2=makeQuery(id+"F0.imprint","INTERSECT",VERTEX,{"derivedFrom":[subQ1,subQ0]});Q72=makeQuery(id+"F0.imprint","IMPRINT",FACE,{"disambiguationData":[TD([[makeQuery(id+"F0.imprint","IMPRINT",EDGE,{"disambiguationData":[TD([[subQ2,-1.0]])],"derivedFrom":subQ1}),1.0]])]});}
            var Q73;
            {var subQ0=sQuery(id+"F0.wireOp",EDGE,"E17");var subQ1=sQuery(id+"F0.wireOp",EDGE,"E0");var subQ2=makeQuery(id+"F0.imprint","INTERSECT",VERTEX,{"derivedFrom":[subQ1,subQ0]});Q73=makeQuery(id+"F0.imprint","IMPRINT",FACE,{"disambiguationData":[TD([[makeQuery(id+"F0.imprint","IMPRINT",EDGE,{"disambiguationData":[TD([[subQ2,-1.0]])],"derivedFrom":subQ1}),1.0]])]});}
            var Q74;
            {var subQ0=sQuery(id+"F0.wireOp",EDGE,"E24");var subQ1=sQuery(id+"F0.wireOp",EDGE,"E0");var subQ2=makeQuery(id+"F0.imprint","INTERSECT",VERTEX,{"derivedFrom":[subQ1,subQ0]});Q74=makeQuery(id+"F0.imprint","IMPRINT",FACE,{"disambiguationData":[TD([[makeQuery(id+"F0.imprint","IMPRINT",EDGE,{"disambiguationData":[TD([[subQ2,-1.0]])],"derivedFrom":subQ1}),1.0]])]});}
            var Q75;
            {var subQ0=sQuery(id+"F0.wireOp",EDGE,"E18");var subQ1=sQuery(id+"F0.wireOp",EDGE,"E0");var subQ2=makeQuery(id+"F0.imprint","INTERSECT",VERTEX,{"derivedFrom":[subQ1,subQ0]});Q75=makeQuery(id+"F0.imprint","IMPRINT",FACE,{"disambiguationData":[TD([[makeQuery(id+"F0.imprint","IMPRINT",EDGE,{"disambiguationData":[TD([[subQ2,-1.0]])],"derivedFrom":subQ1}),1.0]])]});}
            var Q76;
            {var subQ0=sQuery(id+"F0.wireOp",EDGE,"E12");var subQ1=sQuery(id+"F0.wireOp",EDGE,"E0");var subQ2=makeQuery(id+"F0.imprint","INTERSECT",VERTEX,{"derivedFrom":[subQ1,subQ0]});Q76=makeQuery(id+"F0.imprint","IMPRINT",FACE,{"disambiguationData":[TD([[makeQuery(id+"F0.imprint","IMPRINT",EDGE,{"disambiguationData":[TD([[subQ2,-1.0]])],"derivedFrom":subQ1}),1.0]])]});}
            var Q77;
            {var subQ0=sQuery(id+"F0.wireOp",EDGE,"E20");var subQ1=sQuery(id+"F0.wireOp",EDGE,"E0");var subQ2=makeQuery(id+"F0.imprint","INTERSECT",VERTEX,{"derivedFrom":[subQ1,subQ0]});Q77=makeQuery(id+"F0.imprint","IMPRINT",FACE,{"disambiguationData":[TD([[makeQuery(id+"F0.imprint","IMPRINT",EDGE,{"disambiguationData":[TD([[subQ2,-1.0]])],"derivedFrom":subQ1}),1.0]])]});}
            var Q78;
            {var subQ0=sQuery(id+"F0.wireOp",EDGE,"E25");var subQ1=sQuery(id+"F0.wireOp",EDGE,"E0");var subQ2=makeQuery(id+"F0.imprint","INTERSECT",VERTEX,{"derivedFrom":[subQ1,subQ0]});Q78=makeQuery(id+"F0.imprint","IMPRINT",FACE,{"disambiguationData":[TD([[makeQuery(id+"F0.imprint","IMPRINT",EDGE,{"disambiguationData":[TD([[subQ2,-1.0]])],"derivedFrom":subQ1}),1.0]])]});}
            var Q79;
            {var subQ0=sQuery(id+"F0.wireOp",EDGE,"E13");var subQ1=sQuery(id+"F0.wireOp",EDGE,"E0");var subQ2=makeQuery(id+"F0.imprint","INTERSECT",VERTEX,{"derivedFrom":[subQ1,subQ0]});Q79=makeQuery(id+"F0.imprint","IMPRINT",FACE,{"disambiguationData":[TD([[makeQuery(id+"F0.imprint","IMPRINT",EDGE,{"disambiguationData":[TD([[subQ2,1.0]])],"derivedFrom":subQ1}),1.0]])]});}
            var Q80;
            {var subQ0=sQuery(id+"F0.wireOp",EDGE,"E22");var subQ1=sQuery(id+"F0.wireOp",EDGE,"E0");var subQ2=makeQuery(id+"F0.imprint","INTERSECT",VERTEX,{"derivedFrom":[subQ1,subQ0]});Q80=makeQuery(id+"F0.imprint","IMPRINT",FACE,{"disambiguationData":[TD([[makeQuery(id+"F0.imprint","IMPRINT",EDGE,{"disambiguationData":[TD([[subQ2,1.0]])],"derivedFrom":subQ1}),1.0]])]});}
            var Q81;
            {var subQ0=sQuery(id+"F0.wireOp",EDGE,"E21");var subQ1=sQuery(id+"F0.wireOp",EDGE,"E0");var subQ2=makeQuery(id+"F0.imprint","INTERSECT",VERTEX,{"derivedFrom":[subQ1,subQ0]});Q81=makeQuery(id+"F0.imprint","IMPRINT",FACE,{"disambiguationData":[TD([[makeQuery(id+"F0.imprint","IMPRINT",EDGE,{"disambiguationData":[TD([[subQ2,-1.0]])],"derivedFrom":subQ1}),1.0]])]});}
            var Q82;
            {var subQ0=sQuery(id+"F0.wireOp",EDGE,"E23");var subQ1=sQuery(id+"F0.wireOp",EDGE,"E0");var subQ2=makeQuery(id+"F0.imprint","INTERSECT",VERTEX,{"derivedFrom":[subQ1,subQ0]});Q82=makeQuery(id+"F0.imprint","IMPRINT",FACE,{"disambiguationData":[TD([[makeQuery(id+"F0.imprint","IMPRINT",EDGE,{"disambiguationData":[TD([[subQ2,-1.0]])],"derivedFrom":subQ1}),1.0]])]});}
            var Q83;
            {var subQ0=sQuery(id+"F0.wireOp",EDGE,"E22");var subQ1=sQuery(id+"F0.wireOp",EDGE,"E0");var subQ2=makeQuery(id+"F0.imprint","INTERSECT",VERTEX,{"derivedFrom":[subQ1,subQ0]});Q83=makeQuery(id+"F0.imprint","IMPRINT",FACE,{"disambiguationData":[TD([[makeQuery(id+"F0.imprint","IMPRINT",EDGE,{"disambiguationData":[TD([[subQ2,-1.0]])],"derivedFrom":subQ1}),1.0]])]});}
            extrude(context, id + "F1", {"entities" : qUnion([Q0, Q1, Q2, Q3, Q4, Q5, Q6, Q7, Q8, Q9, Q10, Q11, Q12, Q13, Q14, Q15, Q16, Q17, Q18, Q19, Q20, Q21, Q22, Q23, Q24, Q25, Q26, Q27, Q28, Q29, Q30, Q31, Q32, Q33, Q34, Q35, Q36, Q37, Q38, Q39, Q40, Q41, Q42, Q43, Q44, Q45, Q46, Q47, Q48, Q49, Q50, Q51, Q52, Q53, Q54, Q55, Q56, Q57, Q58, Q59, Q60, Q61, Q62, Q63, Q64, Q65, Q66, Q67, Q68, Q69, Q70, Q71, Q72, Q73, Q74, Q75, Q76, Q77, Q78, Q79, Q80, Q81, Q82, Q83]), "depth" : 1.5 * mm, "offsetDistance" : 25.4 * mm});
        }
        {
            var Q0;
            {var subQ1=sQuery(id+"F0.wireOp",EDGE,"E1");var subQ3=sQuery(id+"F0.wireOp",EDGE,"E10");var subQ4=makeQuery(id+"F0.imprint","INTERSECT",VERTEX,{"disambiguationData":[OD(1.0)],"derivedFrom":[subQ1,subQ3]});Q0=makeQuery(id+"F0.imprint","IMPRINT",FACE,{"disambiguationData":[TD([[makeQuery(id+"F0.imprint","IMPRINT",EDGE,{"disambiguationData":[TD([[subQ4,1.0]])],"derivedFrom":subQ3}),1.0]])]});}
            var Q1;
            {var subQ1=sQuery(id+"F0.wireOp",EDGE,"E1");var subQ3=sQuery(id+"F0.wireOp",EDGE,"E10");var subQ4=makeQuery(id+"F0.imprint","INTERSECT",VERTEX,{"disambiguationData":[OD(1.0)],"derivedFrom":[subQ1,subQ3]});Q1=makeQuery(id+"F0.imprint","IMPRINT",FACE,{"disambiguationData":[TD([[makeQuery(id+"F0.imprint","IMPRINT",EDGE,{"disambiguationData":[TD([[subQ4,-1.0]])],"derivedFrom":subQ3}),1.0]])]});}
            var Q2;
            {var subQ1=sQuery(id+"F0.wireOp",EDGE,"E6");var subQ3=sQuery(id+"F0.wireOp",EDGE,"E10");var subQ4=makeQuery(id+"F0.imprint","INTERSECT",VERTEX,{"derivedFrom":[subQ1,subQ3]});Q2=makeQuery(id+"F0.imprint","IMPRINT",FACE,{"disambiguationData":[TD([[makeQuery(id+"F0.imprint","IMPRINT",EDGE,{"disambiguationData":[TD([[subQ4,-1.0]])],"derivedFrom":subQ3}),1.0]])]});}
            var Q3;
            {var subQ1=sQuery(id+"F0.wireOp",EDGE,"E4");var subQ3=sQuery(id+"F0.wireOp",EDGE,"E10");var subQ4=makeQuery(id+"F0.imprint","INTERSECT",VERTEX,{"derivedFrom":[subQ1,subQ3]});Q3=makeQuery(id+"F0.imprint","IMPRINT",FACE,{"disambiguationData":[TD([[makeQuery(id+"F0.imprint","IMPRINT",EDGE,{"disambiguationData":[TD([[subQ4,1.0]])],"derivedFrom":subQ3}),1.0]])]});}
            var Q4;
            {var subQ1=sQuery(id+"F0.wireOp",EDGE,"E1");var subQ3=sQuery(id+"F0.wireOp",EDGE,"E10");var subQ4=makeQuery(id+"F0.imprint","INTERSECT",VERTEX,{"disambiguationData":[OD(0.0)],"derivedFrom":[subQ1,subQ3]});Q4=makeQuery(id+"F0.imprint","IMPRINT",FACE,{"disambiguationData":[TD([[makeQuery(id+"F0.imprint","IMPRINT",EDGE,{"disambiguationData":[TD([[subQ4,1.0]])],"derivedFrom":subQ3}),1.0]])]});}
            var Q5;
            {var subQ1=sQuery(id+"F0.wireOp",EDGE,"E1");var subQ3=sQuery(id+"F0.wireOp",EDGE,"E10");var subQ4=makeQuery(id+"F0.imprint","INTERSECT",VERTEX,{"disambiguationData":[OD(0.0)],"derivedFrom":[subQ1,subQ3]});Q5=makeQuery(id+"F0.imprint","IMPRINT",FACE,{"disambiguationData":[TD([[makeQuery(id+"F0.imprint","IMPRINT",EDGE,{"disambiguationData":[TD([[subQ4,-1.0]])],"derivedFrom":subQ3}),1.0]])]});}
            var Q6;
            {var subQ1=sQuery(id+"F0.wireOp",EDGE,"E1");var subQ3=sQuery(id+"F0.wireOp",EDGE,"E9");var subQ4=makeQuery(id+"F0.imprint","INTERSECT",VERTEX,{"disambiguationData":[OD(0.0)],"derivedFrom":[subQ1,subQ3]});Q6=makeQuery(id+"F0.imprint","IMPRINT",FACE,{"disambiguationData":[TD([[makeQuery(id+"F0.imprint","IMPRINT",EDGE,{"disambiguationData":[TD([[subQ4,1.0]])],"derivedFrom":subQ3}),1.0]])]});}
            var Q7;
            {var subQ1=sQuery(id+"F0.wireOp",EDGE,"E6");var subQ3=sQuery(id+"F0.wireOp",EDGE,"E9");var subQ4=makeQuery(id+"F0.imprint","INTERSECT",VERTEX,{"derivedFrom":[subQ1,subQ3]});Q7=makeQuery(id+"F0.imprint","IMPRINT",FACE,{"disambiguationData":[TD([[makeQuery(id+"F0.imprint","IMPRINT",EDGE,{"disambiguationData":[TD([[subQ4,1.0]])],"derivedFrom":subQ3}),1.0]])]});}
            var Q8;
            {var subQ1=sQuery(id+"F0.wireOp",EDGE,"E5");var subQ3=sQuery(id+"F0.wireOp",EDGE,"E9");var subQ4=makeQuery(id+"F0.imprint","INTERSECT",VERTEX,{"derivedFrom":[subQ1,subQ3]});Q8=makeQuery(id+"F0.imprint","IMPRINT",FACE,{"disambiguationData":[TD([[makeQuery(id+"F0.imprint","IMPRINT",EDGE,{"disambiguationData":[TD([[subQ4,-1.0]])],"derivedFrom":subQ3}),1.0]])]});}
            var Q9;
            {var subQ1=sQuery(id+"F0.wireOp",EDGE,"E1");var subQ3=sQuery(id+"F0.wireOp",EDGE,"E9");var subQ4=makeQuery(id+"F0.imprint","INTERSECT",VERTEX,{"disambiguationData":[OD(1.0)],"derivedFrom":[subQ1,subQ3]});Q9=makeQuery(id+"F0.imprint","IMPRINT",FACE,{"disambiguationData":[TD([[makeQuery(id+"F0.imprint","IMPRINT",EDGE,{"disambiguationData":[TD([[subQ4,-1.0]])],"derivedFrom":subQ3}),1.0]])]});}
            var Q10;
            {var subQ1=sQuery(id+"F0.wireOp",EDGE,"E1");var subQ3=sQuery(id+"F0.wireOp",EDGE,"E9");var subQ4=makeQuery(id+"F0.imprint","INTERSECT",VERTEX,{"disambiguationData":[OD(1.0)],"derivedFrom":[subQ1,subQ3]});Q10=makeQuery(id+"F0.imprint","IMPRINT",FACE,{"disambiguationData":[TD([[makeQuery(id+"F0.imprint","IMPRINT",EDGE,{"disambiguationData":[TD([[subQ4,1.0]])],"derivedFrom":subQ3}),1.0]])]});}
            var Q11;
            {var subQ1=sQuery(id+"F0.wireOp",EDGE,"E1");var subQ3=sQuery(id+"F0.wireOp",EDGE,"E9");var subQ4=makeQuery(id+"F0.imprint","INTERSECT",VERTEX,{"disambiguationData":[OD(0.0)],"derivedFrom":[subQ1,subQ3]});Q11=makeQuery(id+"F0.imprint","IMPRINT",FACE,{"disambiguationData":[TD([[makeQuery(id+"F0.imprint","IMPRINT",EDGE,{"disambiguationData":[TD([[subQ4,-1.0]])],"derivedFrom":subQ3}),1.0]])]});}
            var Q12;
            {var subQ1=sQuery(id+"F0.wireOp",EDGE,"E1");var subQ3=sQuery(id+"F0.wireOp",EDGE,"E8");var subQ4=makeQuery(id+"F0.imprint","INTERSECT",VERTEX,{"disambiguationData":[OD(0.0)],"derivedFrom":[subQ1,subQ3]});Q12=makeQuery(id+"F0.imprint","IMPRINT",FACE,{"disambiguationData":[TD([[makeQuery(id+"F0.imprint","IMPRINT",EDGE,{"disambiguationData":[TD([[subQ4,1.0]])],"derivedFrom":subQ3}),1.0]])]});}
            var Q13;
            {var subQ1=sQuery(id+"F0.wireOp",EDGE,"E5");var subQ3=sQuery(id+"F0.wireOp",EDGE,"E8");var subQ4=makeQuery(id+"F0.imprint","INTERSECT",VERTEX,{"derivedFrom":[subQ1,subQ3]});Q13=makeQuery(id+"F0.imprint","IMPRINT",FACE,{"disambiguationData":[TD([[makeQuery(id+"F0.imprint","IMPRINT",EDGE,{"disambiguationData":[TD([[subQ4,1.0]])],"derivedFrom":subQ3}),1.0]])]});}
            var Q14;
            {var subQ1=sQuery(id+"F0.wireOp",EDGE,"E1");var subQ3=sQuery(id+"F0.wireOp",EDGE,"E8");var subQ4=makeQuery(id+"F0.imprint","INTERSECT",VERTEX,{"disambiguationData":[OD(1.0)],"derivedFrom":[subQ1,subQ3]});Q14=makeQuery(id+"F0.imprint","IMPRINT",FACE,{"disambiguationData":[TD([[makeQuery(id+"F0.imprint","IMPRINT",EDGE,{"disambiguationData":[TD([[subQ4,-1.0]])],"derivedFrom":subQ3}),1.0]])]});}
            var Q15;
            {var subQ1=sQuery(id+"F0.wireOp",EDGE,"E4");var subQ3=sQuery(id+"F0.wireOp",EDGE,"E8");var subQ4=makeQuery(id+"F0.imprint","INTERSECT",VERTEX,{"derivedFrom":[subQ1,subQ3]});Q15=makeQuery(id+"F0.imprint","IMPRINT",FACE,{"disambiguationData":[TD([[makeQuery(id+"F0.imprint","IMPRINT",EDGE,{"disambiguationData":[TD([[subQ4,-1.0]])],"derivedFrom":subQ3}),1.0]])]});}
            var Q16;
            {var subQ1=sQuery(id+"F0.wireOp",EDGE,"E1");var subQ3=sQuery(id+"F0.wireOp",EDGE,"E8");var subQ4=makeQuery(id+"F0.imprint","INTERSECT",VERTEX,{"disambiguationData":[OD(1.0)],"derivedFrom":[subQ1,subQ3]});Q16=makeQuery(id+"F0.imprint","IMPRINT",FACE,{"disambiguationData":[TD([[makeQuery(id+"F0.imprint","IMPRINT",EDGE,{"disambiguationData":[TD([[subQ4,1.0]])],"derivedFrom":subQ3}),1.0]])]});}
            var Q17;
            {var subQ1=sQuery(id+"F0.wireOp",EDGE,"E1");var subQ3=sQuery(id+"F0.wireOp",EDGE,"E8");var subQ4=makeQuery(id+"F0.imprint","INTERSECT",VERTEX,{"disambiguationData":[OD(0.0)],"derivedFrom":[subQ1,subQ3]});Q17=makeQuery(id+"F0.imprint","IMPRINT",FACE,{"disambiguationData":[TD([[makeQuery(id+"F0.imprint","IMPRINT",EDGE,{"disambiguationData":[TD([[subQ4,-1.0]])],"derivedFrom":subQ3}),1.0]])]});}
            var Q18;
            {var subQ0=sQuery(id+"F0.wireOp",EDGE,"E23");var subQ1=sQuery(id+"F0.wireOp",EDGE,"E0");var subQ2=makeQuery(id+"F0.imprint","INTERSECT",VERTEX,{"derivedFrom":[subQ1,subQ0]});Q18=makeQuery(id+"F0.imprint","IMPRINT",FACE,{"disambiguationData":[TD([[makeQuery(id+"F0.imprint","IMPRINT",EDGE,{"disambiguationData":[TD([[subQ2,-1.0]])],"derivedFrom":subQ1}),-1.0]])]});}
            var Q19;
            {var subQ0=sQuery(id+"F0.wireOp",EDGE,"E22");var subQ1=sQuery(id+"F0.wireOp",EDGE,"E0");var subQ2=makeQuery(id+"F0.imprint","INTERSECT",VERTEX,{"derivedFrom":[subQ1,subQ0]});Q19=makeQuery(id+"F0.imprint","IMPRINT",FACE,{"disambiguationData":[TD([[makeQuery(id+"F0.imprint","IMPRINT",EDGE,{"disambiguationData":[TD([[subQ2,-1.0]])],"derivedFrom":subQ1}),-1.0]])]});}
            var Q20;
            {var subQ0=sQuery(id+"F0.wireOp",EDGE,"E22");var subQ1=sQuery(id+"F0.wireOp",EDGE,"E0");var subQ2=makeQuery(id+"F0.imprint","INTERSECT",VERTEX,{"derivedFrom":[subQ1,subQ0]});Q20=makeQuery(id+"F0.imprint","IMPRINT",FACE,{"disambiguationData":[TD([[makeQuery(id+"F0.imprint","IMPRINT",EDGE,{"disambiguationData":[TD([[subQ2,1.0]])],"derivedFrom":subQ1}),-1.0]])]});}
            var Q21;
            {var subQ0=sQuery(id+"F0.wireOp",EDGE,"E21");var subQ1=sQuery(id+"F0.wireOp",EDGE,"E0");var subQ2=makeQuery(id+"F0.imprint","INTERSECT",VERTEX,{"derivedFrom":[subQ1,subQ0]});Q21=makeQuery(id+"F0.imprint","IMPRINT",FACE,{"disambiguationData":[TD([[makeQuery(id+"F0.imprint","IMPRINT",EDGE,{"disambiguationData":[TD([[subQ2,-1.0]])],"derivedFrom":subQ1}),-1.0]])]});}
            var Q22;
            {var subQ0=sQuery(id+"F0.wireOp",EDGE,"E13");var subQ1=sQuery(id+"F0.wireOp",EDGE,"E0");var subQ2=makeQuery(id+"F0.imprint","INTERSECT",VERTEX,{"derivedFrom":[subQ1,subQ0]});Q22=makeQuery(id+"F0.imprint","IMPRINT",FACE,{"disambiguationData":[TD([[makeQuery(id+"F0.imprint","IMPRINT",EDGE,{"disambiguationData":[TD([[subQ2,1.0]])],"derivedFrom":subQ1}),-1.0]])]});}
            var Q23;
            {var subQ0=sQuery(id+"F0.wireOp",EDGE,"E11");var subQ1=sQuery(id+"F0.wireOp",EDGE,"E0");var subQ2=makeQuery(id+"F0.imprint","INTERSECT",VERTEX,{"derivedFrom":[subQ1,subQ0]});Q23=makeQuery(id+"F0.imprint","IMPRINT",FACE,{"disambiguationData":[TD([[makeQuery(id+"F0.imprint","IMPRINT",EDGE,{"disambiguationData":[TD([[subQ2,-1.0]])],"derivedFrom":subQ1}),-1.0]])]});}
            var Q24;
            {var subQ0=sQuery(id+"F0.wireOp",EDGE,"E17");var subQ1=sQuery(id+"F0.wireOp",EDGE,"E0");var subQ2=makeQuery(id+"F0.imprint","INTERSECT",VERTEX,{"derivedFrom":[subQ1,subQ0]});Q24=makeQuery(id+"F0.imprint","IMPRINT",FACE,{"disambiguationData":[TD([[makeQuery(id+"F0.imprint","IMPRINT",EDGE,{"disambiguationData":[TD([[subQ2,-1.0]])],"derivedFrom":subQ1}),-1.0]])]});}
            var Q25;
            {var subQ0=sQuery(id+"F0.wireOp",EDGE,"E24");var subQ1=sQuery(id+"F0.wireOp",EDGE,"E0");var subQ2=makeQuery(id+"F0.imprint","INTERSECT",VERTEX,{"derivedFrom":[subQ1,subQ0]});Q25=makeQuery(id+"F0.imprint","IMPRINT",FACE,{"disambiguationData":[TD([[makeQuery(id+"F0.imprint","IMPRINT",EDGE,{"disambiguationData":[TD([[subQ2,-1.0]])],"derivedFrom":subQ1}),-1.0]])]});}
            var Q26;
            {var subQ0=sQuery(id+"F0.wireOp",EDGE,"E18");var subQ1=sQuery(id+"F0.wireOp",EDGE,"E0");var subQ2=makeQuery(id+"F0.imprint","INTERSECT",VERTEX,{"derivedFrom":[subQ1,subQ0]});Q26=makeQuery(id+"F0.imprint","IMPRINT",FACE,{"disambiguationData":[TD([[makeQuery(id+"F0.imprint","IMPRINT",EDGE,{"disambiguationData":[TD([[subQ2,-1.0]])],"derivedFrom":subQ1}),-1.0]])]});}
            var Q27;
            {var subQ0=sQuery(id+"F0.wireOp",EDGE,"E12");var subQ1=sQuery(id+"F0.wireOp",EDGE,"E0");var subQ2=makeQuery(id+"F0.imprint","INTERSECT",VERTEX,{"derivedFrom":[subQ1,subQ0]});Q27=makeQuery(id+"F0.imprint","IMPRINT",FACE,{"disambiguationData":[TD([[makeQuery(id+"F0.imprint","IMPRINT",EDGE,{"disambiguationData":[TD([[subQ2,-1.0]])],"derivedFrom":subQ1}),-1.0]])]});}
            var Q28;
            {var subQ0=sQuery(id+"F0.wireOp",EDGE,"E20");var subQ1=sQuery(id+"F0.wireOp",EDGE,"E0");var subQ2=makeQuery(id+"F0.imprint","INTERSECT",VERTEX,{"derivedFrom":[subQ1,subQ0]});Q28=makeQuery(id+"F0.imprint","IMPRINT",FACE,{"disambiguationData":[TD([[makeQuery(id+"F0.imprint","IMPRINT",EDGE,{"disambiguationData":[TD([[subQ2,-1.0]])],"derivedFrom":subQ1}),-1.0]])]});}
            var Q29;
            {var subQ0=sQuery(id+"F0.wireOp",EDGE,"E25");var subQ1=sQuery(id+"F0.wireOp",EDGE,"E0");var subQ2=makeQuery(id+"F0.imprint","INTERSECT",VERTEX,{"derivedFrom":[subQ1,subQ0]});Q29=makeQuery(id+"F0.imprint","IMPRINT",FACE,{"disambiguationData":[TD([[makeQuery(id+"F0.imprint","IMPRINT",EDGE,{"disambiguationData":[TD([[subQ2,-1.0]])],"derivedFrom":subQ1}),-1.0]])]});}
            extrude(context, id + "F2", {"entities" : qUnion([Q0, Q1, Q2, Q3, Q4, Q5, Q6, Q7, Q8, Q9, Q10, Q11, Q12, Q13, Q14, Q15, Q16, Q17, Q18, Q19, Q20, Q21, Q22, Q23, Q24, Q25, Q26, Q27, Q28, Q29]), "operationType" : NewBodyOperationType.ADD, "depth" : 5 * mm, "offsetDistance" : 25.4 * mm});
        }
        {
            var Q0;
            Q0=makeQuery(id+"F1.opExtrude","CAP_EDGE",EDGE,{"disambiguationData":[OSD([sQuery(id+"F0.wireOp",EDGE,"E26")])],"isStart":true});
            fillet(context, id + "F3", {"entities" : qUnion([Q0]), "radius" : 2 * mm, "tangentPropagation" : true, "allowEdgeOverflow" : false});
        }
        {
            var Q0;
            {var subQ0=sQuery(id+"F0.wireOp",EDGE,"E11");var subQ1=sQuery(id+"F0.wireOp",EDGE,"E0");var subQ2=makeQuery(id+"F0.imprint","INTERSECT",VERTEX,{"derivedFrom":[subQ1,subQ0]});Q0=makeQuery(id+"F0.imprint","IMPRINT",FACE,{"disambiguationData":[TD([[makeQuery(id+"F0.imprint","IMPRINT",EDGE,{"disambiguationData":[TD([[subQ2,-1.0]])],"derivedFrom":subQ1}),1.0]])]});}
            var Q1;
            {var subQ0=sQuery(id+"F0.wireOp",EDGE,"E23");var subQ1=sQuery(id+"F0.wireOp",EDGE,"E0");var subQ2=makeQuery(id+"F0.imprint","INTERSECT",VERTEX,{"derivedFrom":[subQ1,subQ0]});Q1=makeQuery(id+"F0.imprint","IMPRINT",FACE,{"disambiguationData":[TD([[makeQuery(id+"F0.imprint","IMPRINT",EDGE,{"disambiguationData":[TD([[subQ2,-1.0]])],"derivedFrom":subQ1}),1.0]])]});}
            var Q2;
            {var subQ0=sQuery(id+"F0.wireOp",EDGE,"E22");var subQ1=sQuery(id+"F0.wireOp",EDGE,"E0");var subQ2=makeQuery(id+"F0.imprint","INTERSECT",VERTEX,{"derivedFrom":[subQ1,subQ0]});Q2=makeQuery(id+"F0.imprint","IMPRINT",FACE,{"disambiguationData":[TD([[makeQuery(id+"F0.imprint","IMPRINT",EDGE,{"disambiguationData":[TD([[subQ2,-1.0]])],"derivedFrom":subQ1}),1.0]])]});}
            var Q3;
            {var subQ0=sQuery(id+"F0.wireOp",EDGE,"E22");var subQ1=sQuery(id+"F0.wireOp",EDGE,"E0");var subQ2=makeQuery(id+"F0.imprint","INTERSECT",VERTEX,{"derivedFrom":[subQ1,subQ0]});Q3=makeQuery(id+"F0.imprint","IMPRINT",FACE,{"disambiguationData":[TD([[makeQuery(id+"F0.imprint","IMPRINT",EDGE,{"disambiguationData":[TD([[subQ2,1.0]])],"derivedFrom":subQ1}),1.0]])]});}
            var Q4;
            {var subQ0=sQuery(id+"F0.wireOp",EDGE,"E13");var subQ1=sQuery(id+"F0.wireOp",EDGE,"E0");var subQ2=makeQuery(id+"F0.imprint","INTERSECT",VERTEX,{"derivedFrom":[subQ1,subQ0]});Q4=makeQuery(id+"F0.imprint","IMPRINT",FACE,{"disambiguationData":[TD([[makeQuery(id+"F0.imprint","IMPRINT",EDGE,{"disambiguationData":[TD([[subQ2,1.0]])],"derivedFrom":subQ1}),1.0]])]});}
            var Q5;
            {var subQ0=sQuery(id+"F0.wireOp",EDGE,"E25");var subQ1=sQuery(id+"F0.wireOp",EDGE,"E0");var subQ2=makeQuery(id+"F0.imprint","INTERSECT",VERTEX,{"derivedFrom":[subQ1,subQ0]});Q5=makeQuery(id+"F0.imprint","IMPRINT",FACE,{"disambiguationData":[TD([[makeQuery(id+"F0.imprint","IMPRINT",EDGE,{"disambiguationData":[TD([[subQ2,-1.0]])],"derivedFrom":subQ1}),1.0]])]});}
            var Q6;
            {var subQ0=sQuery(id+"F0.wireOp",EDGE,"E20");var subQ1=sQuery(id+"F0.wireOp",EDGE,"E0");var subQ2=makeQuery(id+"F0.imprint","INTERSECT",VERTEX,{"derivedFrom":[subQ1,subQ0]});Q6=makeQuery(id+"F0.imprint","IMPRINT",FACE,{"disambiguationData":[TD([[makeQuery(id+"F0.imprint","IMPRINT",EDGE,{"disambiguationData":[TD([[subQ2,-1.0]])],"derivedFrom":subQ1}),1.0]])]});}
            var Q7;
            {var subQ0=sQuery(id+"F0.wireOp",EDGE,"E12");var subQ1=sQuery(id+"F0.wireOp",EDGE,"E0");var subQ2=makeQuery(id+"F0.imprint","INTERSECT",VERTEX,{"derivedFrom":[subQ1,subQ0]});Q7=makeQuery(id+"F0.imprint","IMPRINT",FACE,{"disambiguationData":[TD([[makeQuery(id+"F0.imprint","IMPRINT",EDGE,{"disambiguationData":[TD([[subQ2,-1.0]])],"derivedFrom":subQ1}),1.0]])]});}
            var Q8;
            {var subQ0=sQuery(id+"F0.wireOp",EDGE,"E18");var subQ1=sQuery(id+"F0.wireOp",EDGE,"E0");var subQ2=makeQuery(id+"F0.imprint","INTERSECT",VERTEX,{"derivedFrom":[subQ1,subQ0]});Q8=makeQuery(id+"F0.imprint","IMPRINT",FACE,{"disambiguationData":[TD([[makeQuery(id+"F0.imprint","IMPRINT",EDGE,{"disambiguationData":[TD([[subQ2,-1.0]])],"derivedFrom":subQ1}),1.0]])]});}
            var Q9;
            {var subQ0=sQuery(id+"F0.wireOp",EDGE,"E24");var subQ1=sQuery(id+"F0.wireOp",EDGE,"E0");var subQ2=makeQuery(id+"F0.imprint","INTERSECT",VERTEX,{"derivedFrom":[subQ1,subQ0]});Q9=makeQuery(id+"F0.imprint","IMPRINT",FACE,{"disambiguationData":[TD([[makeQuery(id+"F0.imprint","IMPRINT",EDGE,{"disambiguationData":[TD([[subQ2,-1.0]])],"derivedFrom":subQ1}),1.0]])]});}
            var Q10;
            {var subQ0=sQuery(id+"F0.wireOp",EDGE,"E17");var subQ1=sQuery(id+"F0.wireOp",EDGE,"E0");var subQ2=makeQuery(id+"F0.imprint","INTERSECT",VERTEX,{"derivedFrom":[subQ1,subQ0]});Q10=makeQuery(id+"F0.imprint","IMPRINT",FACE,{"disambiguationData":[TD([[makeQuery(id+"F0.imprint","IMPRINT",EDGE,{"disambiguationData":[TD([[subQ2,-1.0]])],"derivedFrom":subQ1}),1.0]])]});}
            var Q11;
            {var subQ0=sQuery(id+"F0.wireOp",EDGE,"E21");var subQ1=sQuery(id+"F0.wireOp",EDGE,"E0");var subQ2=makeQuery(id+"F0.imprint","INTERSECT",VERTEX,{"derivedFrom":[subQ1,subQ0]});Q11=makeQuery(id+"F0.imprint","IMPRINT",FACE,{"disambiguationData":[TD([[makeQuery(id+"F0.imprint","IMPRINT",EDGE,{"disambiguationData":[TD([[subQ2,-1.0]])],"derivedFrom":subQ1}),1.0]])]});}
            extrude(context, id + "F4", {"entities" : qUnion([Q0, Q1, Q2, Q3, Q4, Q5, Q6, Q7, Q8, Q9, Q10, Q11]), "operationType" : NewBodyOperationType.ADD, "depth" : 2.62 * mm, "offsetDistance" : 25.4 * mm});
        }
    });
